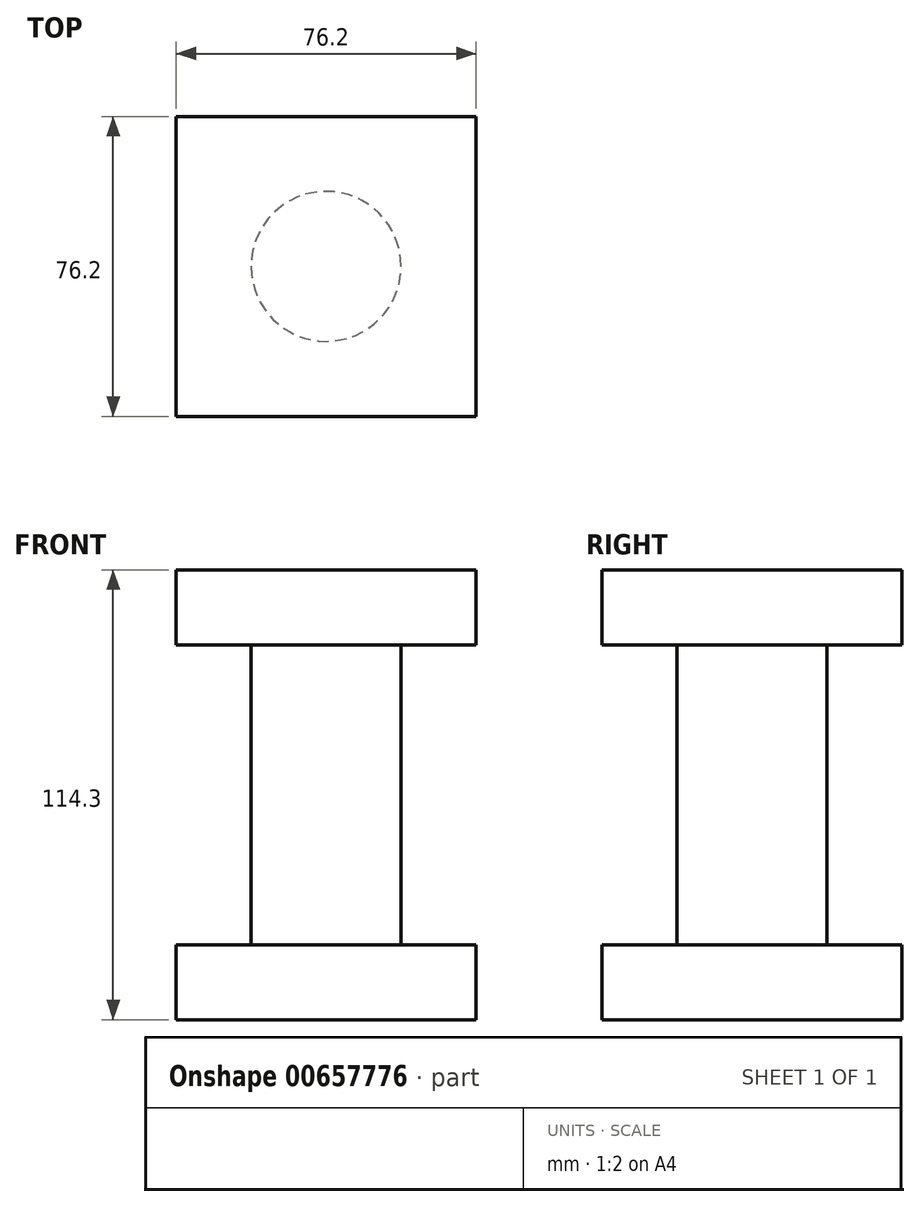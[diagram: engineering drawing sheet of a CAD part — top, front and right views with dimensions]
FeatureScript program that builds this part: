
annotation { "Feature Type Name" : "Feature", "Feature Type Description" : "" }
export const myFeature = defineFeature(function(context is Context, id is Id, definition is map)
    precondition{}
    {
        {
            var Q0;
            Q0=qCreatedBy(makeId("Top.planeOp"),FACE);
            var sketch = newSketch(context, id + "F0", { "sketchPlane" : qUnion([Q0])});
            skLineSegment(sketch, "E0.bottom", {"start": v(38.1, 38.1) * mm, "end": v(-38.1, 38.1) * mm});
            skLineSegment(sketch, "E0.top", {"start": v(38.1, -38.1) * mm, "end": v(-38.1, -38.1) * mm});
            skLineSegment(sketch, "E0.left", {"start": v(38.1, 38.1) * mm, "end": v(38.1, -38.1) * mm});
            skLineSegment(sketch, "E0.right", {"start": v(-38.1, 38.1) * mm, "end": v(-38.1, -38.1) * mm});
            skPoint(sketch, "E0.middle", {"position": v(0, 0) * mm});
            skSolve(sketch);
        }
        {
            var Q0;
            Q0 = qSketchRegion(id + "F0", true);
            extrude(context, id + "F1", {"entities" : qUnion([Q0]), "depth" : 19.05 * mm, "offsetDistance" : 25.4 * mm});
        }
        {
            var Q0;
            Q0=makeQuery(id+"F1.opExtrude","CAP_FACE",FACE,{"disambiguationData":[OSD([sQuery(id+"F0.wireOp",EDGE,"E0.bottom"),sQuery(id+"F0.wireOp",EDGE,"E0.top"),sQuery(id+"F0.wireOp",EDGE,"E0.left"),sQuery(id+"F0.wireOp",EDGE,"E0.right")])],"isStart":false});
            var sketch = newSketch(context, id + "F2", { "sketchPlane" : qUnion([Q0])});
            skCircle(sketch, "E1", {"center": v(0, 0) * mm, "radius": 19.05 * mm});
            skSolve(sketch);
        }
        {
            var Q0;
            Q0 = qSketchRegion(id + "F2", true);
            extrude(context, id + "F3", {"entities" : qUnion([Q0]), "operationType" : NewBodyOperationType.ADD, "depth" : 76.2 * mm, "offsetDistance" : 25.4 * mm});
        }
        {
            var Q0;
            Q0=makeQuery(id+"F3.opExtrude","CAP_FACE",FACE,{"disambiguationData":[OSD([sQuery(id+"F2.wireOp",EDGE,"E1")])],"isStart":false});
            var sketch = newSketch(context, id + "F4", { "sketchPlane" : qUnion([Q0])});
            skLineSegment(sketch, "E2.bottom", {"start": v(38.1, 38.1) * mm, "end": v(-38.1, 38.1) * mm});
            skLineSegment(sketch, "E2.top", {"start": v(38.1, -38.1) * mm, "end": v(-38.1, -38.1) * mm});
            skLineSegment(sketch, "E2.left", {"start": v(38.1, 38.1) * mm, "end": v(38.1, -38.1) * mm});
            skLineSegment(sketch, "E2.right", {"start": v(-38.1, 38.1) * mm, "end": v(-38.1, -38.1) * mm});
            skPoint(sketch, "E2.middle", {"position": v(0, 0) * mm});
            skSolve(sketch);
        }
        {
            var Q0;
            Q0 = qSketchRegion(id + "F4", true);
            extrude(context, id + "F5", {"entities" : qUnion([Q0]), "operationType" : NewBodyOperationType.ADD, "depth" : 19.05 * mm, "offsetDistance" : 25.4 * mm});
        }
    });
